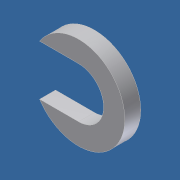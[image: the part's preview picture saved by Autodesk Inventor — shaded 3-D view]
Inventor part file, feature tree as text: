
AUTODESK INVENTOR PART (.ipt)
format: ipt  version: unknown  size: 171,520 bytes
history: native  units: in
note: dims shown in document units (in); Inventor stores cm internally (conversion verified against a paired STEP export)
features: extrude x2, sketch x2
ambient origin geometry x8: Origin, YZ Plane, XZ Plane, XY Plane, X Axis, Y Axis, Z Axis, Center Point
bodies: Solid1 (feature_tree)
feature tree (4):
  extrude  "Extrusion1"  Depth=0.1235in TaperAngle=0.0deg
  extrude  "Extrusion2"  Depth=0.1235in TaperAngle=0.0deg
  sketch  "Sketch1"  dims[d0=0.718in d1=0.1235in d2=0.0in]
  sketch  "Sketch2"  dims[d3=0.39in d4=0.1235in d5=0.0in]
